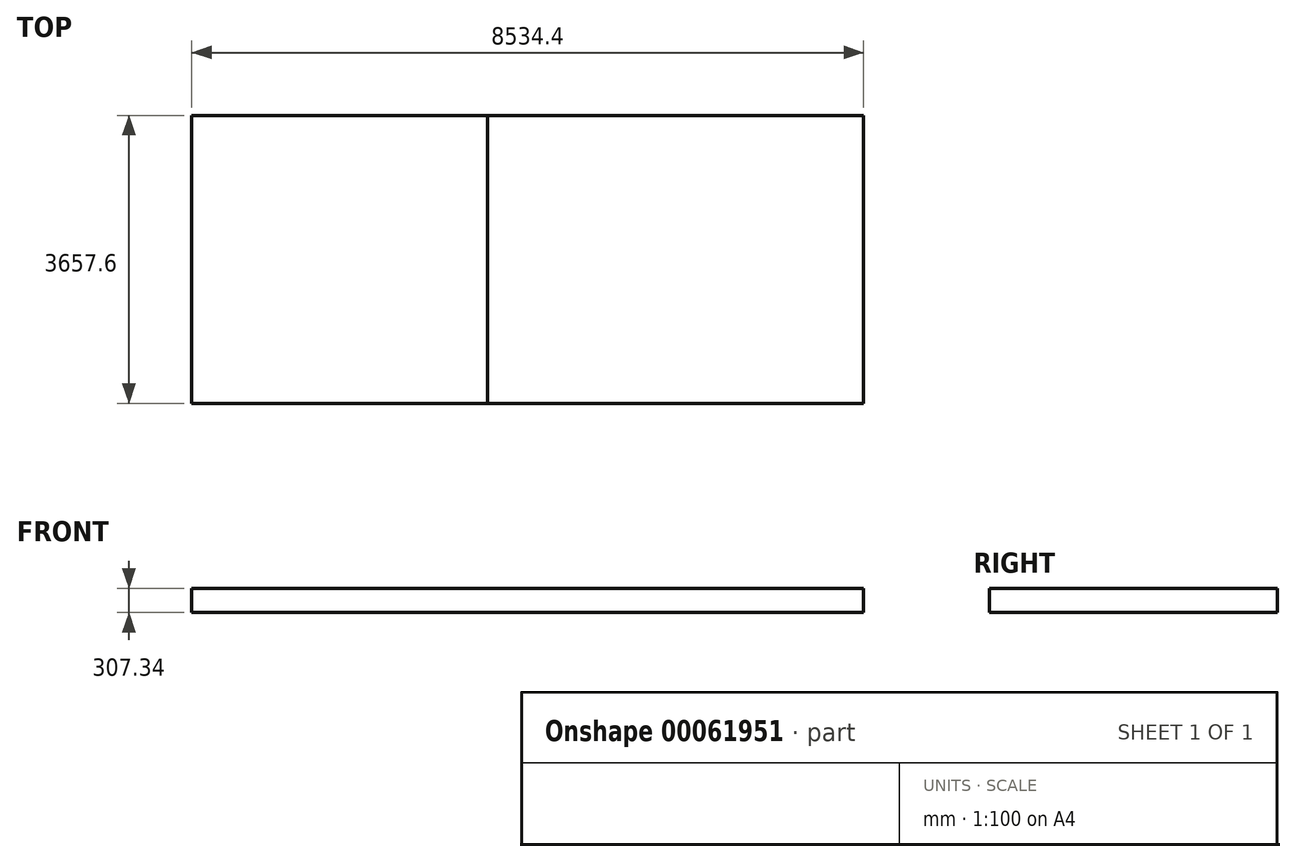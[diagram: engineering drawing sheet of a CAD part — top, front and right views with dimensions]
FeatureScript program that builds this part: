
annotation { "Feature Type Name" : "Feature", "Feature Type Description" : "" }
export const myFeature = defineFeature(function(context is Context, id is Id, definition is map)
    precondition{}
    {
        {
            var Q0;
            Q0=qCreatedBy(makeId("Top.planeOp"),FACE);
            var sketch = newSketch(context, id + "F0", { "sketchPlane" : qUnion([Q0])});
            skLineSegment(sketch, "E0.rect.bottom", {"start": v(4267.2, -1828.8) * mm, "end": v(-4267.2, -1828.8) * mm});
            skLineSegment(sketch, "E0.rect.top", {"start": v(4267.2, 1828.8) * mm, "end": v(-4267.2, 1828.8) * mm});
            skLineSegment(sketch, "E0.rect.left", {"start": v(4267.2, -1828.8) * mm, "end": v(4267.2, 1828.8) * mm});
            skLineSegment(sketch, "E0.rect.right", {"start": v(-4267.2, -1828.8) * mm, "end": v(-4267.2, 1828.8) * mm});
            skPoint(sketch, "E0.rect.middle", {"position": v(0, 0) * mm});
            skSolve(sketch);
        }
        {
            var Q0;
            Q0=makeQuery(id+"F0.imprint","IMPRINT",FACE,{"disambiguationData":[TD([[makeQuery(id+"F0.imprint","IMPRINT",EDGE,{"derivedFrom":sQuery(id+"F0.wireOp",EDGE,"E0.rect.bottom")}),-1.0]])]});
            extrude(context, id + "F1", {"entities" : qUnion([Q0]), "depth" : 304.8 * mm});
        }
        {
            var Q0;
            Q0=makeQuery(id+"F1.opExtrude","CAP_FACE",FACE,{"disambiguationData":[OSD([sQuery(id+"F0.wireOp",EDGE,"E0.rect.bottom"),sQuery(id+"F0.wireOp",EDGE,"E0.rect.top"),sQuery(id+"F0.wireOp",EDGE,"E0.rect.left"),sQuery(id+"F0.wireOp",EDGE,"E0.rect.right")])],"isStart":false});
            var sketch = newSketch(context, id + "F2", { "sketchPlane" : qUnion([Q0])});
            skLineSegment(sketch, "E1.bottom", {"start": v(4267.2, -1828.8) * mm, "end": v(-508, -1828.8) * mm, "construction": true});
            skLineSegment(sketch, "E1.top", {"start": v(4267.2, 1828.8) * mm, "end": v(-508, 1828.8) * mm, "construction": true});
            skLineSegment(sketch, "E1.left", {"start": v(4267.2, -1828.8) * mm, "end": v(4267.2, 1828.8) * mm, "construction": true});
            skLineSegment(sketch, "E1.right", {"start": v(-508, -1828.8) * mm, "end": v(-508, 1828.8) * mm, "construction": true});
            skLineSegment(sketch, "E2.bottom", {"start": v(-4267.2, -1828.8) * mm, "end": v(-508, -1828.8) * mm});
            skLineSegment(sketch, "E2.top", {"start": v(-4267.2, 1828.8) * mm, "end": v(-508, 1828.8) * mm});
            skLineSegment(sketch, "E2.left", {"start": v(-4267.2, -1828.8) * mm, "end": v(-4267.2, 1828.8) * mm});
            skLineSegment(sketch, "E2.right", {"start": v(-508, -1828.8) * mm, "end": v(-508, 1828.8) * mm});
            skSolve(sketch);
        }
        {
            var Q0;
            Q0=makeQuery(id+"F2.imprint","IMPRINT",FACE,{"disambiguationData":[TD([[makeQuery(id+"F2.imprint","IMPRINT",EDGE,{"derivedFrom":sQuery(id+"F2.wireOp",EDGE,"E2.bottom")}),-1.0]])]});
            extrude(context, id + "F3", {"entities" : qUnion([Q0]), "depth" : 2.54 * mm});
        }
    });
